# Revit family: Gira_217600
name_source: partatom
category: Elektroinstallationen
revit_build: Autodesk Revit 2017 (Build: 20160225_1515(x64)
units: mm (PartAtom-declared; Revit-internal decimal feet)

## family parameters
Basisbauteil = Fläche
Beim Laden mit Abzugskörper schneiden = Nein
Bemaßung runder Anschluss = Durchmesser verwenden
Beschriftungsausrichtung beibehalten = Nein
Gemeinsam genutzt = Nein
Raumberechnungspunkt = Nein
Teiletyp = Normal

## types (1)
- Gira_217600
    BIM = https://media.stage.bim.site
    Beschreibung = KNX servo 3 KNX,KNX servo 3,,,Features:,- Electric motor-driven servo with one binary input (zero-voltage) for mounting on thermostat valve bases (recommended: Heimeier) for controlling heating or cooling systems.,- Suitable for room temperature control, e.g. on radiators, convector heaters or heating circuit distributors on floor heating, etc.,- Screwed onto valve head.,- M30 × 1.5 mm connection.,- Integrated bus coupler. The servo is a proportional drive and can be directly integrated into the KNX system (without additional bus coupler).,- Supply voltage is drawn from the KNX system.,- Integrated temperature sensor.,- Integrated room temperature controller.,- Mechanical indicator for valve travel.,- Automatic detection of valve travel.,- One input. This can be used as a binary input or for connecting an external temperature sensor with the following functions:,  Switching, dimming, blind, as dimming value transmitter, as brightness value transmitter, as light scene auxiliary unit with and without memory function, as remote temperature sensor or as temperature limiter for underfloor heating.,- Switching function: two independent switching objects are available for each input (switching commands can parameterised individually), command for leading and trailing edge can be set independently (ON, OFF, CHANGE, no reaction).,- Dimming function: Single and double-surface operation, time between dimming and switching, telegram repetition and stop-telegram transmission possible.,- Blind function: Command can be set with rising edge (no function, UP, DOWN, CHANGE), operating concept can be configured (Step - Move - Step or Move - Step), time between short and long-term operation can be set (only with Step - Move - Step), slat adjustment time can be set.,- Value transmitter function: Edge (button as NO contact, button as NC contact, switch) and value with edge can be configured, value adjustment by pressing and holding a button for value transmitters possible.,- Lighting scenario auxiliary unit with or without memory function.,- Can be used in a heating circuit distributor.,- Protection against jammed valves,- Corrected variable (1 bit or 1 byte).,- Cyclical monitoring of the corrected variable.,- Fault message object for drive faults.,- Emergency operation via internal temperature sensor.,- 2 forced settings or 1 forced setting and 1 limit value object can be set.,- Minimum and maximum variable limit can be set.,,Notes :,- With the default setting, the servo fits on Heimeier valve bases. Use an adapter for valve bases of other manufacturers.
    Bus connection included = Nein
    Bus system KNX = Ja
    Bus system KNX radio = Nein
    Bus system LON = Nein
    Bus system Powernet = Nein
    Bus system radio frequent = Nein
    Data sheet = https://katalog.gira.de
    Degree of protection (IP) = IP20
    GTIN = 4010337019374
    HAN = 217600
    Hersteller = Gira
    Mounting method = Radiator valve
    Other bus systems = None
    Productwebsite = http://katalog.gira.de
    Radio frequent bidirectional = Nein
    Typname = Servo 3 KNX
    URL = https://www.gira.de
    Vorgabe-Ansicht = 1219 mm

## geometry (parser evidence)
native form markers: Sweep x3
no freeform markers — native parametric forms only
